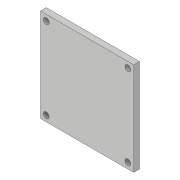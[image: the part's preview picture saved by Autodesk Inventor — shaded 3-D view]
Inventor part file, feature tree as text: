
AUTODESK INVENTOR PART (.ipt)
format: ipt  version: 2019 (Build 230136000, 136)  size: 92,672 bytes
history: native  units: in
note: dims shown in document units (in); Inventor stores cm internally (conversion verified against a paired STEP export)
features: extrude x2, sketch x2
ambient origin geometry x8: Origin, YZ Plane, XZ Plane, XY Plane, X Axis, Y Axis, Z Axis, Center Point
bodies: Solid1 (feature_tree)
feature tree (4):
  extrude  "Extrusion1"  Depth=6.2992in
  extrude  "Extrusion2"  Depth=0.3937in
  sketch  "Sketch1"  dims[d0=6.2992in d1=6.2992in]
  sketch  "Sketch2"  dims[d2=0.3937in d3=0.0in d4=0.3937in d5=0.3937in d6=5.5118in d7=5.5118in d8=5.5118in d9=5.5118in d10=0.3937in d11=0.3937in d12=0.3937in d13=0.3937in d14=0.0in d15=0.0in]
